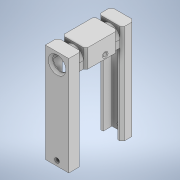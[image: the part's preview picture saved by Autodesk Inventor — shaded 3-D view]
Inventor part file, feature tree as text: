
AUTODESK INVENTOR PART (.ipt)
format: ipt  version: 2021 (Build 250183000, 183)  size: 259,072 bytes
history: native  units: mm
features: sketch x7, extrude x6, plane x2, mirror x2, chamfer x2, projected_geometry x2, revolve x1, fillet x1, direct_edit x1, move_body x1
ambient origin geometry x8: Origin, YZ Plane, XZ Plane, XY Plane, X Axis, Y Axis, Z Axis, Center Point
bodies: Solid1 (feature_tree)
feature tree (25):
  extrude  "Extrusion1"  Depth=10.0mm
  extrude  "Extrusion3"  Depth=45.0mm TaperAngle=0.0deg
  extrude  "Extrusion4"  Depth=40.0mm TaperAngle=0.0deg
  plane  "Work Plane3"
  revolve  "Revolution1"  [1 undecoded]
  fillet  "Fillet1"  [1 undecoded]
  mirror  "Mirror1"
  plane  "Work Plane2"
  extrude  "Extrusion5"  Depth=3.0mm
  chamfer  "Chamfer4"  Distance=8.0mm
  mirror  "Mirror2"
  chamfer  "Chamfer5"  [1 undecoded]
  extrude  "Extrusion6"  Depth=3.0mm TaperAngle=0.0deg
  extrude  "Extrusion8"  Depth=5.0mm
  direct_edit  "Direct Edit1"
  sketch  "Sketch1"  dims[d0=10.0mm d3=60.0mm]
  sketch  "Sketch3"  dims[d4=16.0mm d5=45.0mm d6=0.0mm]
  sketch  "Sketch4"  dims[d21=40.0mm d22=60.0mm d23=0.0mm]
  sketch  "Sketch5"  dims[d26=110.0mm d27=0.0mm d35=1.8mm d40=90.0deg]
  sketch  "Sketch6"  dims[d41=1.0mm d42=3.0mm]
  sketch  "Sketch7"  dims[d43=0.75mm]
  sketch  "Sketch9"  dims[d44=2.5mm d45=8.0mm d46=-10.0mm d48=3.0mm d49=0.0mm d50=5.0mm d51=1.5mm d52=2.0mm d53=45.0deg d54=20.0mm d55=1.0mm d56=2.0mm d57=45.0deg d58=3.4mm d59=3.2mm d60=0.0mm d61=0.0mm d66=113.0mm d67=0.0mm d68=8.0mm d69=1.5mm d70=-24.9mm d71=0.0mm d72=0.0mm d73=-0.25mm d75=1.8mm]
  projected_geometry  "Projected Loop2"
  projected_geometry  "Projected Loop3"
  move_body  "Move1"
note: 3 required parameter values undecoded (feature->parameter linkage not recoverable at this tier; creation-order binding heuristic only, values carry confidence <= 0.55)